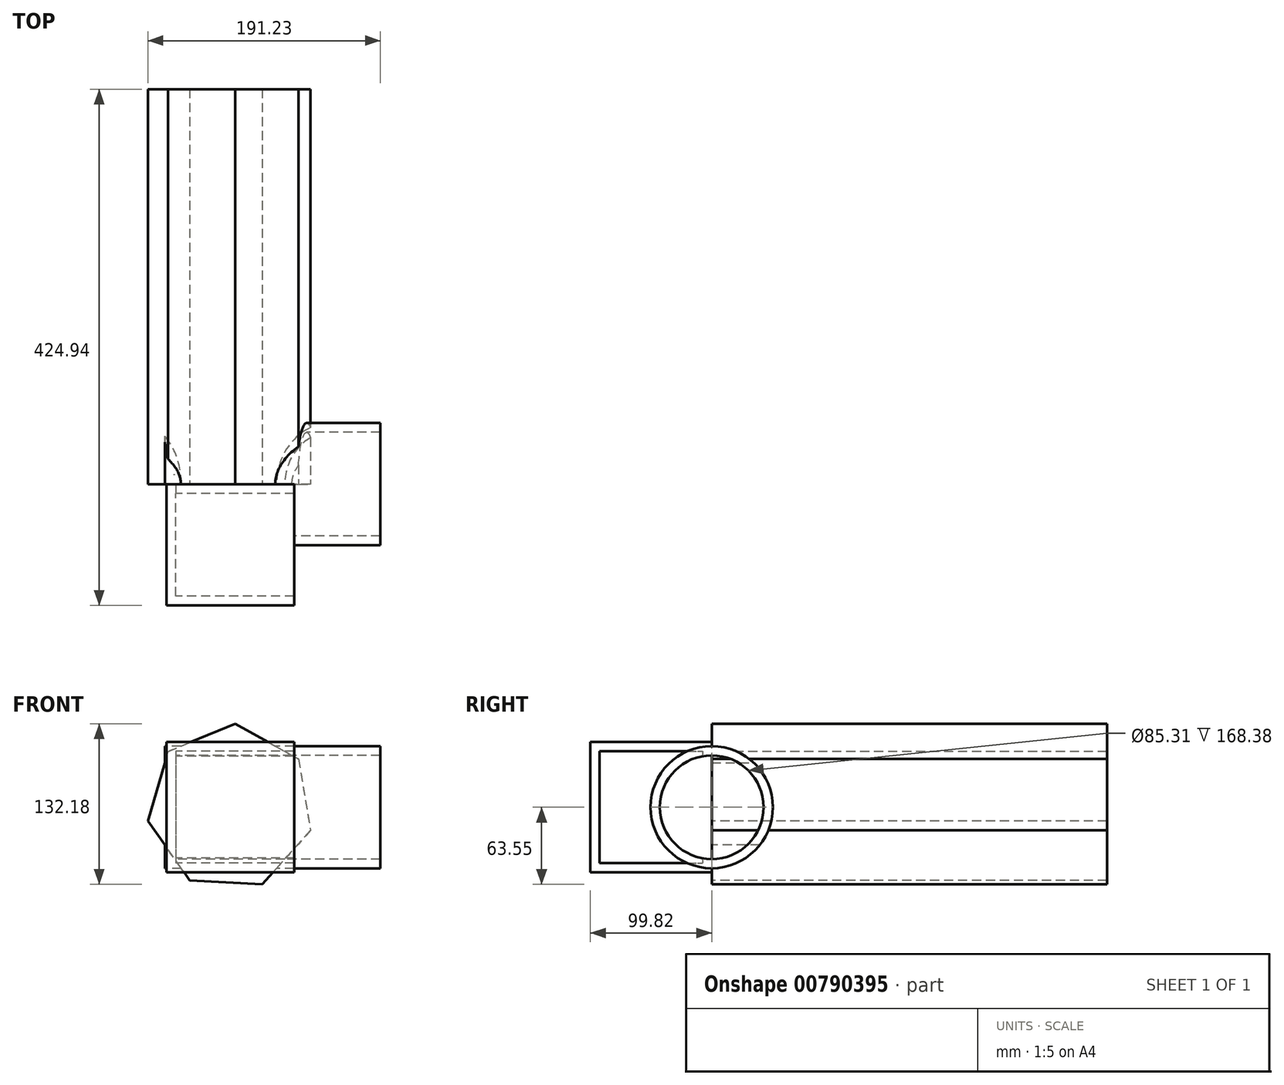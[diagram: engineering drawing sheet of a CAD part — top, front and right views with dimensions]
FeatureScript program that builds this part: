
annotation { "Feature Type Name" : "Feature", "Feature Type Description" : "" }
export const myFeature = defineFeature(function(context is Context, id is Id, definition is map)
    precondition{}
    {
        {
            var Q0;
            Q0=qCreatedBy(makeId("Front.planeOp"),FACE);
            var sketch = newSketch(context, id + "F0", { "sketchPlane" : qUnion([Q0])});
            skLineSegment(sketch, "E0.bottom", {"start": v(52.56, 53.68) * mm, "end": v(-52.56, 53.68) * mm});
            skLineSegment(sketch, "E0.top", {"start": v(52.56, -53.68) * mm, "end": v(-52.56, -53.68) * mm});
            skLineSegment(sketch, "E0.left", {"start": v(52.56, 53.68) * mm, "end": v(52.56, -53.68) * mm});
            skLineSegment(sketch, "E0.right", {"start": v(-52.56, 53.68) * mm, "end": v(-52.56, -53.68) * mm});
            skPoint(sketch, "E0.middle", {"position": v(0, 0) * mm});
            skSolve(sketch);
        }
        {
            var Q0;
            Q0=makeQuery(id+"F0.imprint","IMPRINT",FACE,{"disambiguationData":[TD([[makeQuery(id+"F0.imprint","IMPRINT",EDGE,{"derivedFrom":sQuery(id+"F0.wireOp",EDGE,"E0.bottom")}),1.0]])]});
            extrude(context, id + "F1", {"entities" : qUnion([Q0]), "depth" : 99.82 * mm, "offsetDistance" : 25.4 * mm});
        }
        {
            var Q0;
            Q0=qCreatedBy(makeId("Right.planeOp"),FACE);
            var sketch = newSketch(context, id + "F2", { "sketchPlane" : qUnion([Q0])});
            skCircle(sketch, "E1", {"center": v(0, 0) * mm, "radius": 50.28 * mm});
            skSolve(sketch);
        }
        {
            var Q0;
            Q0=makeQuery(id+"F2.imprint","IMPRINT",FACE,{"disambiguationData":[TD([[makeQuery(id+"F2.imprint","IMPRINT",EDGE,{"derivedFrom":sQuery(id+"F2.wireOp",EDGE,"E1")}),1.0]])]});
            extrude(context, id + "F3", {"entities" : qUnion([Q0]), "operationType" : NewBodyOperationType.ADD, "depth" : 123.44 * mm, "offsetDistance" : 25.4 * mm});
        }
        {
            var Q0;
            Q0=makeQuery(id+"F3.opExtrude","CAP_FACE",FACE,{"disambiguationData":[OSD([sQuery(id+"F2.wireOp",EDGE,"E1")])],"isStart":true});
            extrude(context, id + "F4", {"entities" : qUnion([Q0]), "operationType" : NewBodyOperationType.ADD, "depth" : 53.85 * mm, "offsetDistance" : 25.4 * mm});
        }
        {
            var Q0;
            Q0=makeQuery(id+"F1.opExtrude","SWEPT_FACE",FACE,{"disambiguationData":[OSD([sQuery(id+"F0.wireOp",EDGE,"E0.left")])]});
            var Q1;
            Q1=makeQuery(id+"F3.opExtrude","CAP_FACE",FACE,{"disambiguationData":[OSD([sQuery(id+"F2.wireOp",EDGE,"E1")])],"isStart":false});
            shell(context, id + "F5", {"entities" : qUnion([Q0, Q1]), "thickness" : 7.62 * mm});
        }
        {
            var Q0;
            Q0=qCreatedBy(makeId("Front.planeOp"),FACE);
            var sketch = newSketch(context, id + "F6", { "sketchPlane" : qUnion([Q0])});
            skCircle(sketch, "E2.cCircle", {"center": v(0, 0) * mm, "radius": 68.75 * mm, "construction": true});
            skLineSegment(sketch, "E2.0", {"start": v(-51.2, 45.88) * mm, "end": v(3.95, 68.63) * mm});
            skLineSegment(sketch, "E2.1", {"start": v(3.95, 68.63) * mm, "end": v(56.12, 39.7) * mm});
            skLineSegment(sketch, "E2.2", {"start": v(56.12, 39.7) * mm, "end": v(66.03, -19.12) * mm});
            skLineSegment(sketch, "E2.3", {"start": v(66.03, -19.12) * mm, "end": v(26.22, -63.55) * mm});
            skLineSegment(sketch, "E2.4", {"start": v(26.22, -63.55) * mm, "end": v(-33.34, -60.12) * mm});
            skLineSegment(sketch, "E2.5", {"start": v(-33.34, -60.12) * mm, "end": v(-67.8, -11.42) * mm});
            skLineSegment(sketch, "E2.6", {"start": v(-67.8, -11.42) * mm, "end": v(-51.2, 45.88) * mm});
            skSolve(sketch);
        }
        {
            var Q0;
            Q0=makeQuery(id+"F6.imprint","IMPRINT",FACE,{"disambiguationData":[TD([[makeQuery(id+"F6.imprint","IMPRINT",EDGE,{"derivedFrom":sQuery(id+"F6.wireOp",EDGE,"E2.0")}),-1.0]])]});
            extrude(context, id + "F7", {"entities" : qUnion([Q0]), "operationType" : NewBodyOperationType.ADD, "oppositeDirection" : true, "depth" : 325.12 * mm, "offsetDistance" : 25.4 * mm});
        }
    });
